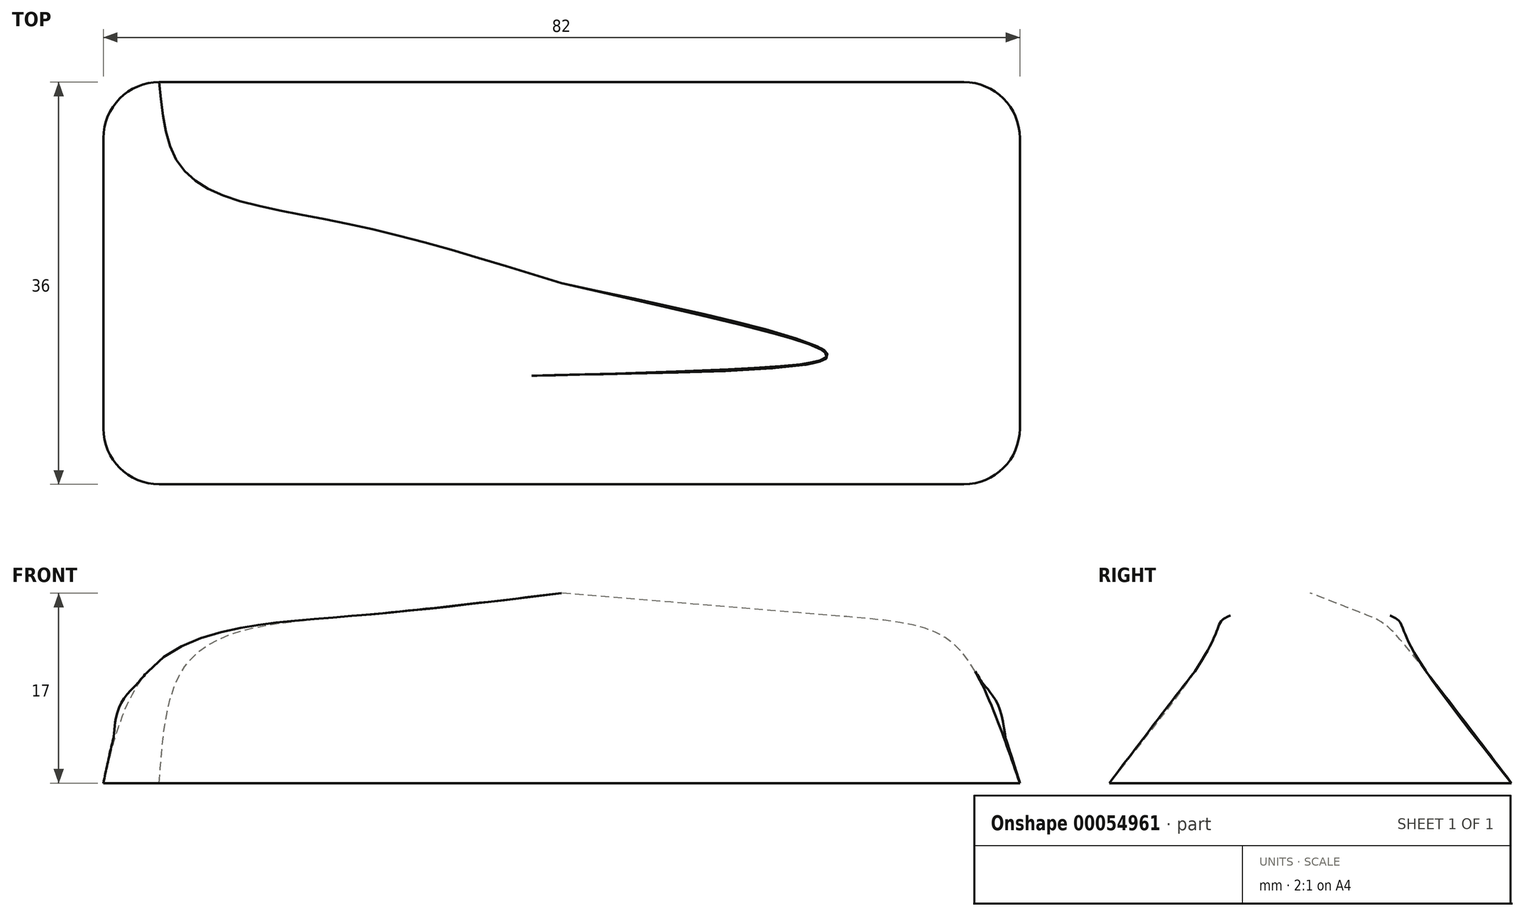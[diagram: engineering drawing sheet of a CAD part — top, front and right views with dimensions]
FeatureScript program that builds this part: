
annotation { "Feature Type Name" : "Feature", "Feature Type Description" : "" }
export const myFeature = defineFeature(function(context is Context, id is Id, definition is map)
    precondition{}
    {
        {
            var Q0;
            Q0=qCreatedBy(makeId("Top.planeOp"),FACE);
            var sketch = newSketch(context, id + "F0", { "sketchPlane" : qUnion([Q0])});
            skLineSegment(sketch, "E0.bottom", {"start": v(-41, 23) * mm, "end": v(41, 23) * mm});
            skLineSegment(sketch, "E0.top", {"start": v(-41, -23) * mm, "end": v(41, -23) * mm});
            skLineSegment(sketch, "E0.left", {"start": v(-46, 18) * mm, "end": v(-46, -18) * mm});
            skLineSegment(sketch, "E0.right", {"start": v(46, 18) * mm, "end": v(46, -18) * mm});
            skLineSegment(sketch, "E1.0", {"start": v(-36, 18) * mm, "end": v(36, 18) * mm});
            skLineSegment(sketch, "E1.1", {"start": v(-41, 13) * mm, "end": v(-41, -13) * mm});
            skLineSegment(sketch, "E1.2", {"start": v(-36, -18) * mm, "end": v(36, -18) * mm});
            skLineSegment(sketch, "E1.3", {"start": v(41, 13) * mm, "end": v(41, -13) * mm});
            skPoint(sketch, "E2.visualSharp", {"position": v(-41, 18) * mm});
            skArc(sketch, "E2.filletArc", {"start": v(-36, 18) * mm, "mid": v(-39.54, 16.54) * mm, "end": v(-41, 13) * mm});
            skPoint(sketch, "E3.visualSharp", {"position": v(41, 18) * mm});
            skArc(sketch, "E3.filletArc", {"start": v(41, 13) * mm, "mid": v(39.54, 16.54) * mm, "end": v(36, 18) * mm});
            skPoint(sketch, "E4.visualSharp", {"position": v(41, -18) * mm});
            skArc(sketch, "E4.filletArc", {"start": v(36, -18) * mm, "mid": v(39.54, -16.54) * mm, "end": v(41, -13) * mm});
            skPoint(sketch, "E5.visualSharp", {"position": v(-41, -18) * mm});
            skArc(sketch, "E5.filletArc", {"start": v(-41, -13) * mm, "mid": v(-39.54, -16.54) * mm, "end": v(-36, -18) * mm});
            skPoint(sketch, "E6.visualSharp", {"position": v(-46, 23) * mm});
            skArc(sketch, "E6.filletArc", {"start": v(-41, 23) * mm, "mid": v(-44.54, 21.54) * mm, "end": v(-46, 18) * mm});
            skPoint(sketch, "E7.visualSharp", {"position": v(46, -23) * mm});
            skArc(sketch, "E7.filletArc", {"start": v(41, -23) * mm, "mid": v(44.54, -21.54) * mm, "end": v(46, -18) * mm});
            skPoint(sketch, "E8.visualSharp", {"position": v(46, 23) * mm});
            skArc(sketch, "E8.filletArc", {"start": v(46, 18) * mm, "mid": v(44.54, 21.54) * mm, "end": v(41, 23) * mm});
            skPoint(sketch, "E9.visualSharp", {"position": v(-46, -23) * mm});
            skArc(sketch, "E9.filletArc", {"start": v(-46, -18) * mm, "mid": v(-44.54, -21.54) * mm, "end": v(-41, -23) * mm});
            skSolve(sketch);
        }
        {
            var Q0;
            Q0=qCreatedBy(makeId("Top.planeOp"),FACE);
            cPlane(context, id + "F1", {"entities" : qUnion([Q0]), "cplaneType" : CPlaneType.OFFSET, "offset" : 10 * mm, "width" : 150 * mm, "height" : 150 * mm});
        }
        {
            var Q0;
            Q0=qCreatedBy(id+"F1.planeOp",FACE);
            var sketch = newSketch(context, id + "F2", { "sketchPlane" : qUnion([Q0])});
            skLineSegment(sketch, "E10", {"start": v(-41, 13) * mm, "end": v(0, 0) * mm, "construction": true});
            skLineSegment(sketch, "E11", {"start": v(0, 0) * mm, "end": v(39.38, -17.3) * mm, "construction": true});
            skLineSegment(sketch, "E12", {"start": v(-37, 0) * mm, "end": v(0, 0) * mm, "construction": true});
            skLineSegment(sketch, "E13", {"start": v(0, 0) * mm, "end": v(37, 0) * mm, "construction": true});
            skLineSegment(sketch, "E14.0.MirrorCS", {"start": v(-41, -13) * mm, "end": v(0, 0) * mm, "construction": true});
            skLineSegment(sketch, "E15.0.MirrorCS", {"start": v(0, 0) * mm, "end": v(39.38, 17.3) * mm, "construction": true});
            skLineSegment(sketch, "E16", {"start": v(-20.5, 6.5) * mm, "end": v(-21.1, 4.6) * mm});
            skFitSpline(sketch, "E17", {"points": [v(0, 0) * mm, v(-21.1, 4.6) * mm, v(-41, 13) * mm], "startDerivative": vector(-18, 0) * mm, "endDerivative": vector(0, 9) * mm, "construction": true});
            skFitSpline(sketch, "E18.0.MirrorCS", {"points": [v(0, 0) * mm, v(-21.1, -4.6) * mm, v(-41, -13) * mm], "startDerivative": vector(-18, 0) * mm, "endDerivative": vector(0, -9) * mm, "construction": true});
            skFitSpline(sketch, "E19.0.MirrorCS", {"points": [v(0, 0) * mm, v(21.1, -4.6) * mm, v(41, -13) * mm], "startDerivative": vector(18, 0) * mm, "endDerivative": vector(0, -9) * mm, "construction": true});
            skFitSpline(sketch, "E19.1.MirrorCS", {"points": [v(0, 0) * mm, v(21.1, 4.6) * mm, v(41, 13) * mm], "startDerivative": vector(18, 0) * mm, "endDerivative": vector(0, 9) * mm, "construction": true});
            skLineSegment(sketch, "E20.bottom", {"start": v(-34, 10.34) * mm, "end": v(34, 10.34) * mm});
            skLineSegment(sketch, "E20.top", {"start": v(-34, -10.34) * mm, "end": v(34, -10.34) * mm});
            skLineSegment(sketch, "E20.left", {"start": v(-37, 7.34) * mm, "end": v(-37, -7.34) * mm});
            skLineSegment(sketch, "E20.right", {"start": v(37, 7.34) * mm, "end": v(37, -7.34) * mm});
            skLineSegment(sketch, "E21.bottom", {"start": v(-21.1, 4.6) * mm, "end": v(21.1, 4.6) * mm, "construction": true});
            skLineSegment(sketch, "E21.top", {"start": v(-21.1, -4.6) * mm, "end": v(21.1, -4.6) * mm, "construction": true});
            skLineSegment(sketch, "E21.left", {"start": v(-21.1, 4.6) * mm, "end": v(-21.1, -4.6) * mm, "construction": true});
            skLineSegment(sketch, "E21.right", {"start": v(21.1, 4.6) * mm, "end": v(21.1, -4.6) * mm, "construction": true});
            skPoint(sketch, "E22.visualSharp", {"position": v(-37, -10.34) * mm});
            skArc(sketch, "E22.filletArc", {"start": v(-37, -7.34) * mm, "mid": v(-36.12, -9.46) * mm, "end": v(-34, -10.34) * mm});
            skPoint(sketch, "E23.visualSharp", {"position": v(37, 10.34) * mm});
            skArc(sketch, "E23.filletArc", {"start": v(37, 7.34) * mm, "mid": v(36.12, 9.46) * mm, "end": v(34, 10.34) * mm});
            skPoint(sketch, "E24.visualSharp", {"position": v(37, -10.34) * mm});
            skArc(sketch, "E24.filletArc", {"start": v(34, -10.34) * mm, "mid": v(36.12, -9.46) * mm, "end": v(37, -7.34) * mm});
            skPoint(sketch, "E25.visualSharp", {"position": v(-37, 10.34) * mm});
            skArc(sketch, "E25.filletArc", {"start": v(-34, 10.34) * mm, "mid": v(-36.12, 9.46) * mm, "end": v(-37, 7.34) * mm});
            skSolve(sketch);
        }
        {
            var Q0;
            Q0=qCreatedBy(id+"F1.planeOp",FACE);
            cPlane(context, id + "F3", {"entities" : qUnion([Q0]), "cplaneType" : CPlaneType.OFFSET, "offset" : 5 * mm, "width" : 150 * mm, "height" : 150 * mm});
        }
        {
            var Q0;
            Q0=qCreatedBy(id+"F3.planeOp",FACE);
            var sketch = newSketch(context, id + "F4", { "sketchPlane" : qUnion([Q0])});
            skLineSegment(sketch, "E26.bottom", {"start": v(-16.28, 7.14) * mm, "end": v(22.3, 7.14) * mm});
            skLineSegment(sketch, "E26.top", {"start": v(-16.28, -7.17) * mm, "end": v(22.3, -7.17) * mm});
            skLineSegment(sketch, "E26.left", {"start": v(-18.28, 5.14) * mm, "end": v(-18.28, -5.17) * mm});
            skLineSegment(sketch, "E26.right", {"start": v(24.3, 5.14) * mm, "end": v(24.3, -5.17) * mm});
            skPoint(sketch, "E27.visualSharp", {"position": v(-18.28, 7.14) * mm});
            skArc(sketch, "E27.filletArc", {"start": v(-16.28, 7.14) * mm, "mid": v(-17.7, 6.56) * mm, "end": v(-18.28, 5.14) * mm});
            skPoint(sketch, "E28.visualSharp", {"position": v(24.3, 7.14) * mm});
            skArc(sketch, "E28.filletArc", {"start": v(24.3, 5.14) * mm, "mid": v(23.72, 6.56) * mm, "end": v(22.3, 7.14) * mm});
            skPoint(sketch, "E29.visualSharp", {"position": v(24.3, -7.17) * mm});
            skArc(sketch, "E29.filletArc", {"start": v(22.3, -7.17) * mm, "mid": v(23.72, -6.58) * mm, "end": v(24.3, -5.17) * mm});
            skPoint(sketch, "E30.visualSharp", {"position": v(-18.28, -7.17) * mm});
            skArc(sketch, "E30.filletArc", {"start": v(-18.28, -5.17) * mm, "mid": v(-17.7, -6.58) * mm, "end": v(-16.28, -7.17) * mm});
            skSolve(sketch);
        }
        {
            var Q0;
            Q0=qCreatedBy(id+"F3.planeOp",FACE);
            cPlane(context, id + "F5", {"entities" : qUnion([Q0]), "cplaneType" : CPlaneType.OFFSET, "offset" : 2 * mm, "width" : 150 * mm, "height" : 150 * mm});
        }
        {
            var Q0;
            Q0=qCreatedBy(id+"F5.planeOp",FACE);
            var sketch = newSketch(context, id + "F6", { "sketchPlane" : qUnion([Q0])});
            skPoint(sketch, "E31", {"position": v(0, 0) * mm});
            skSolve(sketch);
        }
        {
            var Q0;
            Q0=makeQuery(id+"F0.imprint","IMPRINT",FACE,{"disambiguationData":[TD([[makeQuery(id+"F0.imprint","IMPRINT",EDGE,{"derivedFrom":sQuery(id+"F0.wireOp",EDGE,"E1.0")}),-1.0]])]});
            var Q1;
            Q1=makeQuery(id+"F0.imprint","IMPRINT",FACE,{"disambiguationData":[TD([[makeQuery(id+"F0.imprint","IMPRINT",EDGE,{"derivedFrom":sQuery(id+"F0.wireOp",EDGE,"E1.0")}),-1.0]])]});
            var Q2;
            Q2=makeQuery(id+"F2.imprint","IMPRINT",FACE,{"disambiguationData":[TD([[makeQuery(id+"F2.imprint","IMPRINT",EDGE,{"derivedFrom":sQuery(id+"F2.wireOp",EDGE,"E20.bottom")}),-1.0]])]});
            var Q3;
            Q3=makeQuery(id+"F4.imprint","IMPRINT",FACE,{"disambiguationData":[TD([[makeQuery(id+"F4.imprint","IMPRINT",EDGE,{"derivedFrom":sQuery(id+"F4.wireOp",EDGE,"E26.bottom")}),-1.0]])]});
            var Q4;
            Q4=sQuery(id+"F6.wireOp",VERTEX,"E31");
            loft(context, id + "F7", {"bodyType" : ToolBodyType.SURFACE, "sheetProfilesArray" : [{ "sheetProfileEntities" : qUnion([Q0]) }], "wireProfilesArray" : [{ "wireProfileEntities" : qUnion([Q1]) }, { "wireProfileEntities" : qUnion([Q2]) }, { "wireProfileEntities" : qUnion([Q3]) }, { "wireProfileEntities" : qUnion([Q4]) }]});
        }
    });
